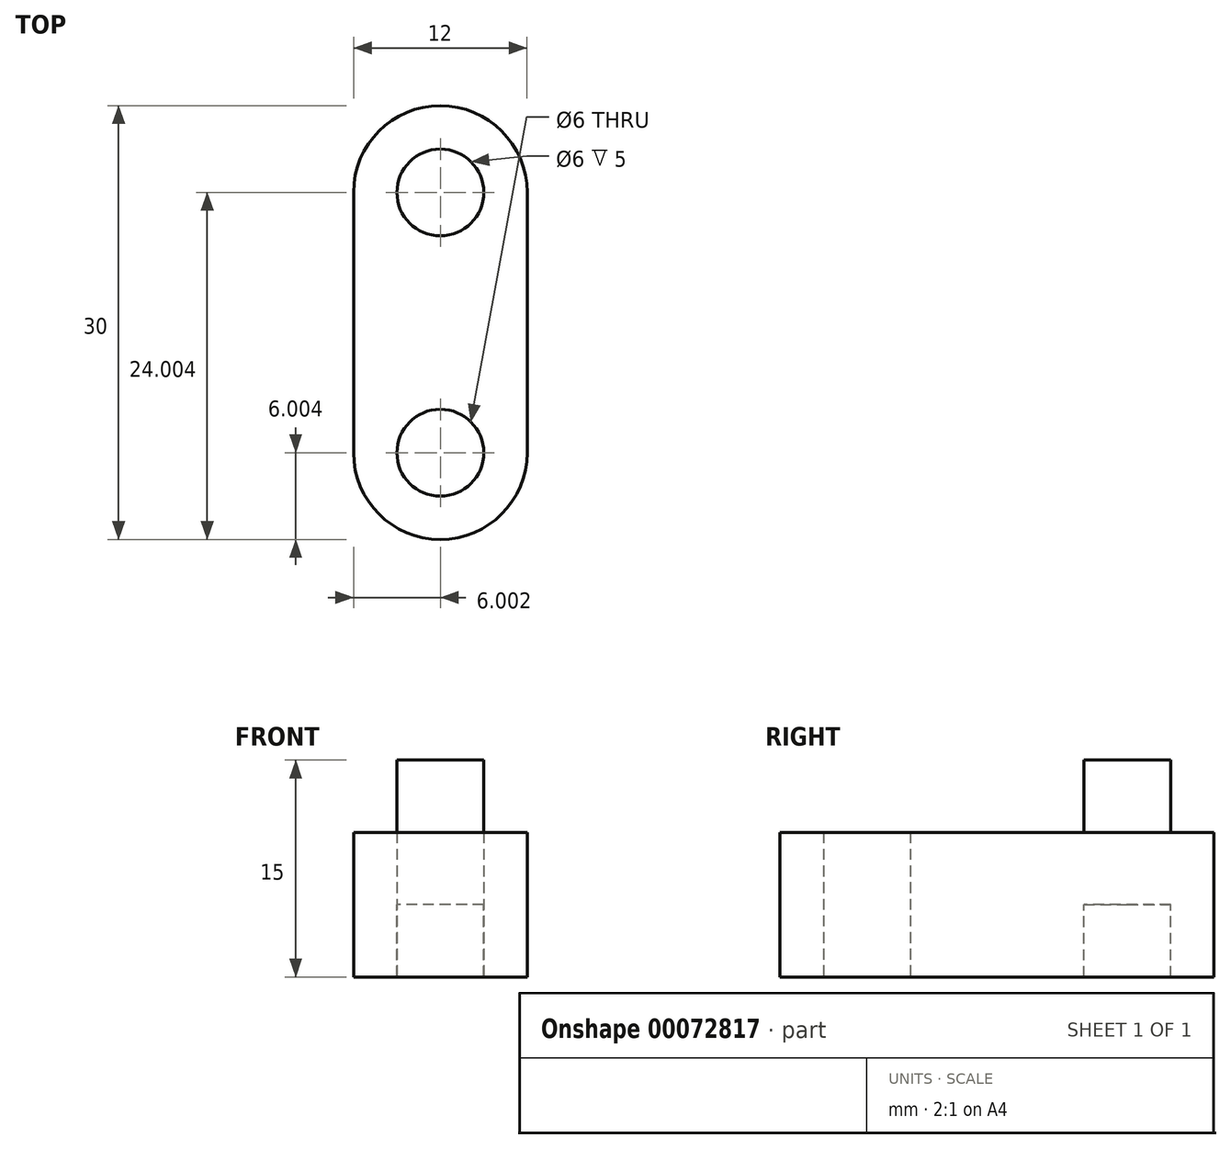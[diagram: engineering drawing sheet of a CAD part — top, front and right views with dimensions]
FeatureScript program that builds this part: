
annotation { "Feature Type Name" : "Feature", "Feature Type Description" : "" }
export const myFeature = defineFeature(function(context is Context, id is Id, definition is map)
    precondition{}
    {
        {
            var Q0;
            Q0=qCreatedBy(makeId("Top.planeOp"),FACE);
            var sketch = newSketch(context, id + "F0", { "sketchPlane" : qUnion([Q0])});
            skLineSegment(sketch, "E0.rect.bottom", {"start": v(6.01, 14.56) * mm, "end": v(-5.99, 14.56) * mm});
            skLineSegment(sketch, "E0.rect.top", {"start": v(6.01, -15.44) * mm, "end": v(-5.99, -15.44) * mm});
            skLineSegment(sketch, "E0.rect.left", {"start": v(6.01, 14.56) * mm, "end": v(6.01, -15.44) * mm});
            skLineSegment(sketch, "E0.rect.right", {"start": v(-5.99, 14.56) * mm, "end": v(-5.99, -15.44) * mm});
            skPoint(sketch, "E0.rect.middle", {"position": v(0.01, -0.44) * mm});
            skCircle(sketch, "E1", {"center": v(0.01, 8.56) * mm, "radius": 3 * mm});
            skLineSegment(sketch, "E2", {"start": v(-43.39, -0.44) * mm, "end": v(6.34, -0.44) * mm, "construction": true});
            skPoint(sketch, "E2.endSnap0", {"position": v(-5.99, -0.44) * mm});
            skCircle(sketch, "E3.MirrorC", {"center": v(0.01, -9.44) * mm, "radius": 3 * mm});
            skSolve(sketch);
        }
        {
            var Q0;
            Q0=makeQuery(id+"F0.imprint","IMPRINT",FACE,{"disambiguationData":[TD([[makeQuery(id+"F0.imprint","IMPRINT",EDGE,{"derivedFrom":sQuery(id+"F0.wireOp",EDGE,"E0.rect.bottom")}),1.0]])]});
            var Q1;
            Q1=makeQuery(id+"F0.imprint","IMPRINT",FACE,{"disambiguationData":[TD([[makeQuery(id+"F0.imprint","IMPRINT",EDGE,{"derivedFrom":sQuery(id+"F0.wireOp",EDGE,"E1")}),1.0]])]});
            var Q2;
            Q2=makeQuery(id+"F0.imprint","IMPRINT",FACE,{"disambiguationData":[TD([[makeQuery(id+"F0.imprint","IMPRINT",EDGE,{"derivedFrom":sQuery(id+"F0.wireOp",EDGE,"E3.MirrorC")}),-1.0]])]});
            extrude(context, id + "F1", {"entities" : qUnion([Q0, Q1, Q2]), "depth" : 5 * mm});
        }
        {
            var Q0;
            Q0=makeQuery(id+"F0.imprint","IMPRINT",FACE,{"disambiguationData":[TD([[makeQuery(id+"F0.imprint","IMPRINT",EDGE,{"derivedFrom":sQuery(id+"F0.wireOp",EDGE,"E1")}),1.0]])]});
            var Q1;
            Q1=sQuery(id+"F0.wireOp",EDGE,"E1");
            extrude(context, id + "F2", {"entities" : qUnion([Q0]), "operationType" : NewBodyOperationType.ADD, "surfaceEntities" : qUnion([Q1]), "depth" : 10 * mm});
        }
        {
            var Q0;
            Q0=makeQuery(id+"F0.imprint","IMPRINT",FACE,{"disambiguationData":[TD([[makeQuery(id+"F0.imprint","IMPRINT",EDGE,{"derivedFrom":sQuery(id+"F0.wireOp",EDGE,"E3.MirrorC")}),-1.0]])]});
            extrude(context, id + "F3", {"entities" : qUnion([Q0]), "operationType" : NewBodyOperationType.ADD, "oppositeDirection" : true, "depth" : 5 * mm});
        }
        {
            var Q0;
            Q0=makeQuery(id+"F1.opExtrude","SWEPT_EDGE",EDGE,{"disambiguationData":[OSD([sQuery(id+"F0.wireOp",EDGE,"E0.rect.bottom"),sQuery(id+"F0.wireOp",EDGE,"E0.rect.left")])]});
            var Q1;
            Q1=makeQuery(id+"F1.opExtrude","SWEPT_EDGE",EDGE,{"disambiguationData":[OSD([sQuery(id+"F0.wireOp",EDGE,"E0.rect.bottom"),sQuery(id+"F0.wireOp",EDGE,"E0.rect.right")])]});
            var Q2;
            Q2=makeQuery(id+"F1.opExtrude","SWEPT_EDGE",EDGE,{"disambiguationData":[OSD([sQuery(id+"F0.wireOp",EDGE,"E0.rect.top"),sQuery(id+"F0.wireOp",EDGE,"E0.rect.left")])]});
            var Q3;
            Q3=makeQuery(id+"F1.opExtrude","SWEPT_EDGE",EDGE,{"disambiguationData":[OSD([sQuery(id+"F0.wireOp",EDGE,"E0.rect.top"),sQuery(id+"F0.wireOp",EDGE,"E0.rect.right")])]});
            fillet(context, id + "F4", {"entities" : qUnion([Q0, Q1, Q2, Q3]), "radius" : 6 * mm, "tangentPropagation" : true, "allowEdgeOverflow" : false});
        }
    });
